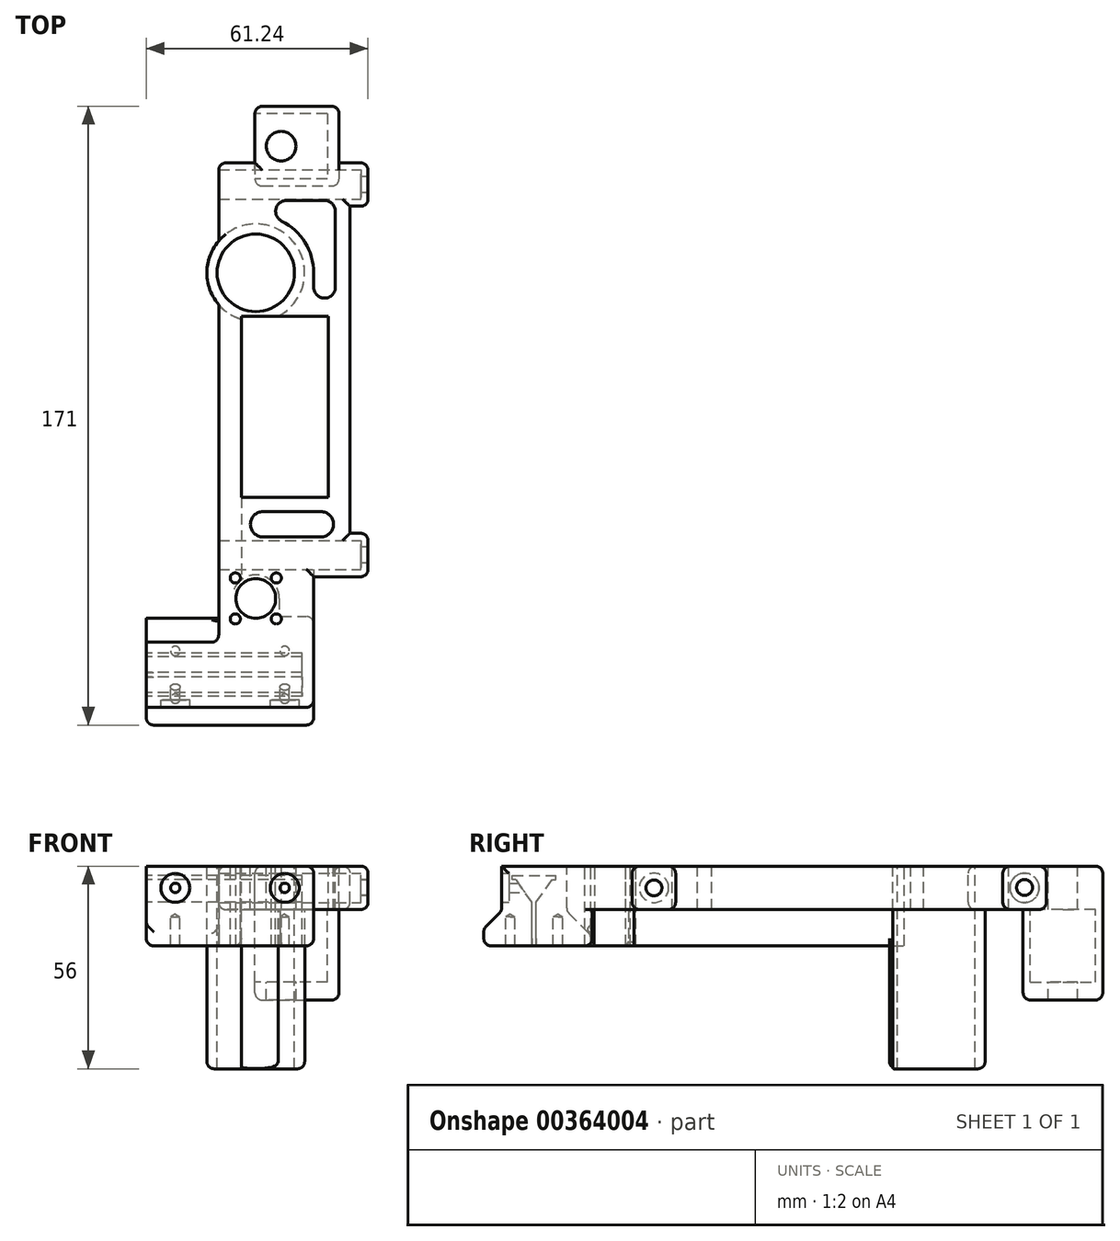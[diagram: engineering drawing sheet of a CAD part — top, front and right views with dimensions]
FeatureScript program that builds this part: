
annotation { "Feature Type Name" : "Feature", "Feature Type Description" : "" }
export const myFeature = defineFeature(function(context is Context, id is Id, definition is map)
    precondition{}
    {
        {
            var Q0;
            Q0=qCreatedBy(makeId("Top.planeOp"),FACE);
            var sketch = newSketch(context, id + "F0", { "sketchPlane" : qUnion([Q0])});
            skLineSegment(sketch, "E0", {"start": v(0, 0) * mm, "end": v(0, -35) * mm});
            skLineSegment(sketch, "E1.bottom", {"start": v(-30, 25) * mm, "end": v(-6, 25) * mm});
            skLineSegment(sketch, "E1.top", {"start": v(-30, -25) * mm, "end": v(-6, -25) * mm});
            skLineSegment(sketch, "E1.left", {"start": v(-30, 25) * mm, "end": v(-30, -25) * mm});
            skLineSegment(sketch, "E1.right", {"start": v(-6, 25) * mm, "end": v(-6, -25) * mm});
            skCircle(sketch, "E2", {"center": v(-26, 37) * mm, "radius": 10.7 * mm});
            skCircle(sketch, "E3", {"center": v(-26, -53) * mm, "radius": 5.5 * mm});
            skLineSegment(sketch, "E4", {"start": v(-10, -47) * mm, "end": v(-10, -88) * mm});
            skLineSegment(sketch, "E5", {"start": v(0, -35) * mm, "end": v(3, -35) * mm});
            skLineSegment(sketch, "E6", {"start": v(3, -35) * mm, "end": v(3, -47) * mm});
            skLineSegment(sketch, "E7", {"start": v(3, -47) * mm, "end": v(-10, -47) * mm});
            skLineSegment(sketch, "E8", {"start": v(3, 67.4) * mm, "end": v(3, 55.4) * mm});
            skLineSegment(sketch, "E9", {"start": v(3, 55.4) * mm, "end": v(0, 55.4) * mm});
            skLineSegment(sketch, "E10", {"start": v(0, 55.4) * mm, "end": v(0, 0) * mm});
            skLineSegment(sketch, "E11", {"start": v(3, 61.4) * mm, "end": v(-99.75, 61.4) * mm, "construction": true});
            skArc(sketch, "E12", {"start": v(-36.24, 28.2) * mm, "mid": v(-39.5, 37) * mm, "end": v(-36.24, 45.8) * mm});
            skLineSegment(sketch, "E13", {"start": v(-36.24, -53) * mm, "end": v(-36.24, 28.2) * mm});
            skLineSegment(sketch, "E14", {"start": v(-36.24, 45.8) * mm, "end": v(-36.24, 67.4) * mm});
            skLineSegment(sketch, "E15", {"start": v(-26.24, 83) * mm, "end": v(-3, 83) * mm});
            skLineSegment(sketch, "E16", {"start": v(-3, 83) * mm, "end": v(-3, 67.4) * mm});
            skLineSegment(sketch, "E17", {"start": v(-3, 67.4) * mm, "end": v(3, 67.4) * mm});
            skLineSegment(sketch, "E18", {"start": v(-36.24, 67.4) * mm, "end": v(-26.24, 67.4) * mm});
            skLineSegment(sketch, "E19", {"start": v(-26.24, 67.4) * mm, "end": v(-26.24, 83) * mm});
            skLineSegment(sketch, "E20", {"start": v(-10, -88) * mm, "end": v(-56.24, -88) * mm});
            skLineSegment(sketch, "E21", {"start": v(-56.24, -88) * mm, "end": v(-56.24, -53) * mm});
            skLineSegment(sketch, "E22", {"start": v(-56.24, -53) * mm, "end": v(-36.24, -53) * mm});
            skLineSegment(sketch, "E23", {"start": v(3, -41) * mm, "end": v(-100.11, -41) * mm, "construction": true});
            skCircle(sketch, "E24", {"center": v(-20.34, -47.34) * mm, "radius": 1.4 * mm});
            skLineSegment(sketch, "E25", {"start": v(-26, -53) * mm, "end": v(-20.34, -47.34) * mm, "construction": true});
            skCircle(sketch, "E26.1.0", {"center": v(-31.66, -47.34) * mm, "radius": 1.4 * mm});
            skLineSegment(sketch, "E26.1.1", {"start": v(-26, -53) * mm, "end": v(-31.66, -47.34) * mm, "construction": true});
            skCircle(sketch, "E26.2.0", {"center": v(-31.66, -58.66) * mm, "radius": 1.4 * mm});
            skLineSegment(sketch, "E26.2.1", {"start": v(-26, -53) * mm, "end": v(-31.66, -58.66) * mm, "construction": true});
            skCircle(sketch, "E26.3.0", {"center": v(-20.34, -58.66) * mm, "radius": 1.4 * mm});
            skLineSegment(sketch, "E26.3.1", {"start": v(-26, -53) * mm, "end": v(-20.34, -58.66) * mm, "construction": true});
            skLineSegment(sketch, "E27.bottom", {"start": v(-24, -36) * mm, "end": v(-8, -36) * mm});
            skLineSegment(sketch, "E27.top", {"start": v(-24, -29) * mm, "end": v(-8, -29) * mm});
            skArc(sketch, "E28", {"start": v(-24, -36) * mm, "mid": v(-27.5, -32.5) * mm, "end": v(-24, -29) * mm});
            skArc(sketch, "E29", {"start": v(-8, -36) * mm, "mid": v(-4.5, -32.5) * mm, "end": v(-8, -29) * mm});
            skArc(sketch, "E30", {"start": v(-4.04, 33.46) * mm, "mid": v(-6.77, 30) * mm, "end": v(-10, 33) * mm});
            skLineSegment(sketch, "E31", {"start": v(-10, 33) * mm, "end": v(-10, 37) * mm});
            skLineSegment(sketch, "E32", {"start": v(-4.04, 33.46) * mm, "end": v(-4.04, 54) * mm});
            skArc(sketch, "E33", {"start": v(-18.85, 51.32) * mm, "mid": v(-20.43, 54.69) * mm, "end": v(-17.51, 57) * mm});
            skLineSegment(sketch, "E34", {"start": v(-17.51, 57) * mm, "end": v(-7.04, 57) * mm});
            skArc(sketch, "E35", {"start": v(-7.04, 57) * mm, "mid": v(-4.91, 56.12) * mm, "end": v(-4.04, 54) * mm});
            skArc(sketch, "E36", {"start": v(-18.85, 51.32) * mm, "mid": v(-12.4, 45.42) * mm, "end": v(-10, 37) * mm});
            skCircle(sketch, "E37", {"center": v(-19, 72) * mm, "radius": 4.1 * mm});
            skSolve(sketch);
        }
        {
            var Q0;
            Q0=qSketchRegion(id+"F0",true);
            extrude(context, id + "F1", {"entities" : qUnion([Q0]), "oppositeDirection" : true, "depth" : 12 * mm, "offsetDistance" : 25 * mm});
        }
        {
            var Q0;
            Q0=makeQuery(id+"F1.opExtrude","SWEPT_FACE",FACE,{"disambiguationData":[OSD([sQuery(id+"F0.wireOp",EDGE,"E6")])]});
            var sketch = newSketch(context, id + "F2", { "sketchPlane" : qUnion([Q0])});
            skCircle(sketch, "E38", {"center": v(-41, -6) * mm, "radius": 4.05 * mm});
            skPoint(sketch, "E38.centerSnap0", {"position": v(-41, 0) * mm});
            skPoint(sketch, "E38.centerSnap1", {"position": v(-47, -6) * mm});
            skCircle(sketch, "E39", {"center": v(61.4, -6) * mm, "radius": 4.05 * mm});
            skPoint(sketch, "E39.centerSnap0", {"position": v(-35, -6) * mm});
            skSolve(sketch);
        }
        {
            var Q0;
            Q0=qSketchRegion(id+"F2",true);
            extrude(context, id + "F3", {"entities" : qUnion([Q0]), "operationType" : NewBodyOperationType.REMOVE, "endBound" : BoundingType.THROUGH_ALL, "oppositeDirection" : true, "depth" : 25 * mm});
        }
        {
            var Q0;
            Q0=makeQuery(id+"F1.opExtrude","SWEPT_FACE",FACE,{"disambiguationData":[OSD([sQuery(id+"F0.wireOp",EDGE,"E6")])]});
            var sketch = newSketch(context, id + "F4", { "sketchPlane" : qUnion([Q0])});
            skLineSegment(sketch, "E40.bottom", {"start": v(-47, 0) * mm, "end": v(-35, 0) * mm});
            skLineSegment(sketch, "E40.top", {"start": v(-47, -12) * mm, "end": v(-35, -12) * mm});
            skLineSegment(sketch, "E40.left", {"start": v(-47, 0) * mm, "end": v(-47, -12) * mm});
            skLineSegment(sketch, "E40.right", {"start": v(-35, 0) * mm, "end": v(-35, -12) * mm});
            skLineSegment(sketch, "E41.bottom", {"start": v(55.4, -12) * mm, "end": v(67.4, -12) * mm});
            skLineSegment(sketch, "E41.top", {"start": v(55.4, 0) * mm, "end": v(67.4, 0) * mm});
            skLineSegment(sketch, "E41.left", {"start": v(55.4, -12) * mm, "end": v(55.4, 0) * mm});
            skLineSegment(sketch, "E41.right", {"start": v(67.4, -12) * mm, "end": v(67.4, 0) * mm});
            skCircle(sketch, "E42", {"center": v(-41, -6) * mm, "radius": 2.2 * mm});
            skCircle(sketch, "E43", {"center": v(61.4, -5.9) * mm, "radius": 2.2 * mm});
            skSolve(sketch);
        }
        {
            var Q0;
            Q0=qSketchRegion(id+"F4",true);
            extrude(context, id + "F5", {"entities" : qUnion([Q0]), "operationType" : NewBodyOperationType.ADD, "depth" : 2 * mm});
        }
        {
            var Q0;
            Q0=makeQuery(id+"F5.boolean.opBoolean","MERGE",FACE,{"derivedFrom":[makeQuery(id+"F1.opExtrude","CAP_FACE",FACE,{"disambiguationData":[OSD([sQuery(id+"F0.wireOp",EDGE,"E0"),sQuery(id+"F0.wireOp",EDGE,"E1.bottom"),sQuery(id+"F0.wireOp",EDGE,"E1.top"),sQuery(id+"F0.wireOp",EDGE,"E1.left"),sQuery(id+"F0.wireOp",EDGE,"E1.right"),sQuery(id+"F0.wireOp",EDGE,"E2"),sQuery(id+"F0.wireOp",EDGE,"E3"),sQuery(id+"F0.wireOp",EDGE,"XIlzzrbo-8YrF-T5Wf-SoYO-HWZPlr7hWIC8"),sQuery(id+"F0.wireOp",EDGE,"E4"),sQuery(id+"F0.wireOp",EDGE,"E5"),sQuery(id+"F0.wireOp",EDGE,"E6"),sQuery(id+"F0.wireOp",EDGE,"E7"),sQuery(id+"F0.wireOp",EDGE,"2jG298rw-YP8h-8Yay-5vSP-wDqkU1IMKlhE"),sQuery(id+"F0.wireOp",EDGE,"E8"),sQuery(id+"F0.wireOp",EDGE,"E9"),sQuery(id+"F0.wireOp",EDGE,"E10"),sQuery(id+"F0.wireOp",EDGE,"SC18iBPG-TUrN-Iioa-Ju5e-pfgaNuiYKQF4"),sQuery(id+"F0.wireOp",EDGE,"QfddEPE0-9GQP-GPq8-b5eB-5ln1efAZQpw0"),sQuery(id+"F0.wireOp",EDGE,"7sLd4AGe-hb9Z-zQUN-UB1L-9xo2n5h3wb6e")])],"isStart":false}),makeQuery(id+"F5.opExtrude","SWEPT_FACE",FACE,{"disambiguationData":[OSD([sQuery(id+"F4.wireOp",EDGE,"E40.top")])]}),makeQuery(id+"F5.opExtrude","SWEPT_FACE",FACE,{"disambiguationData":[OSD([sQuery(id+"F4.wireOp",EDGE,"E41.bottom")])]})]});
            var sketch = newSketch(context, id + "F6", { "sketchPlane" : qUnion([Q0])});
            skLineSegment(sketch, "E44", {"start": v(-19.82, -25) * mm, "end": v(-30, -25) * mm});
            skCircle(sketch, "E45", {"center": v(-26, -37) * mm, "radius": 10.7 * mm});
            skLineSegment(sketch, "E46", {"start": v(-36.24, -28.2) * mm, "end": v(-36.24, -28.2) * mm});
            skArc(sketch, "E47", {"start": v(-19.82, -25) * mm, "mid": v(-23.42, -50.25) * mm, "end": v(-36.24, -28.2) * mm});
            skLineSegment(sketch, "E48", {"start": v(-36.24, -28.2) * mm, "end": v(-36.24, 53) * mm});
            skLineSegment(sketch, "E49", {"start": v(-36.24, 53) * mm, "end": v(-56.24, 53) * mm});
            skLineSegment(sketch, "E50", {"start": v(-56.24, 53) * mm, "end": v(-56.24, 88) * mm});
            skLineSegment(sketch, "E51", {"start": v(-56.24, 88) * mm, "end": v(-10, 88) * mm});
            skLineSegment(sketch, "E52", {"start": v(-10, 88) * mm, "end": v(-10, 58) * mm});
            skLineSegment(sketch, "E53", {"start": v(-30, 47.88) * mm, "end": v(-30, -25) * mm});
            skCircle(sketch, "E54", {"center": v(-26, 53) * mm, "radius": 5.5 * mm});
            skArc(sketch, "E55", {"start": v(-30, 47.88) * mm, "mid": v(-23.15, 47.16) * mm, "end": v(-19.5, 53) * mm});
            skLineSegment(sketch, "E56", {"start": v(-19.5, 53) * mm, "end": v(-19.5, 57.54) * mm});
            skLineSegment(sketch, "E57", {"start": v(-19.1, 58) * mm, "end": v(-10, 58) * mm});
            skCircle(sketch, "E58", {"center": v(-31.66, 58.66) * mm, "radius": 1.4 * mm});
            skCircle(sketch, "E59", {"center": v(-31.66, 47.34) * mm, "radius": 1.4 * mm});
            skArc(sketch, "E60", {"start": v(-19.5, 57.54) * mm, "mid": v(-21.4, 59.57) * mm, "end": v(-19.1, 58) * mm});
            skSolve(sketch);
        }
        {
            var Q0;
            Q0=qSketchRegion(id+"F6",true);
            extrude(context, id + "F7", {"entities" : qUnion([Q0]), "operationType" : NewBodyOperationType.ADD, "depth" : 10 * mm, "offsetDistance" : 25 * mm});
        }
        {
            var Q0;
            Q0=makeQuery(id+"F7.opExtrude","CAP_FACE",FACE,{"disambiguationData":[OSD([sQuery(id+"F6.wireOp",EDGE,"6GX7EmJv-jwu0-vBWY-FxLW-R2JSKk5cSaNS"),sQuery(id+"F6.wireOp",EDGE,"E44"),sQuery(id+"F6.wireOp",EDGE,"hchj6tDb-mTsj-hI8Y-6XvQ-siWjQFpiHixI"),sQuery(id+"F6.wireOp",EDGE,"jRI5jhwU-Cl4Y-UO73-bT4B-RttWuhhWPOQr"),sQuery(id+"F6.wireOp",EDGE,"E45"),sQuery(id+"F6.wireOp",EDGE,"EboCQFRa-d3EB-sAKS-RsI5-4XPLM2VXSoXr"),sQuery(id+"F6.wireOp",EDGE,"GLrA7Uhn-oGKT-5vrt-4Lsz-RlGKhm1cIkbv"),sQuery(id+"F6.wireOp",EDGE,"iAbHuVxw-Mz87-is6H-xszH-xwFxznPorsnN"),sQuery(id+"F6.wireOp",EDGE,"boATnbXS-9fhP-6PQb-uzRW-Yihyjwh3bqXk"),sQuery(id+"F6.wireOp",EDGE,"SkgAi7Z9-kDo3-rvMO-CMYk-elsrKzZPDKzr"),sQuery(id+"F6.wireOp",EDGE,"9utY1JgT-HuLY-Yqt8-Up9m-p6niSZGJffs8"),sQuery(id+"F6.wireOp",EDGE,"Q8Ah0BUv-GUdk-BIgZ-kX4k-YRNa6w1N2wjC"),sQuery(id+"F6.wireOp",EDGE,"4O1aqaJq-Fub8-MtC8-jOK8-P5grKxW9meOc"),sQuery(id+"F6.wireOp",EDGE,"lIdf07tD-03wC-Cnkd-RmJ2-D04lD4p26Tqx"),sQuery(id+"F6.wireOp",EDGE,"E46")])],"isStart":false});
            var sketch = newSketch(context, id + "F8", { "sketchPlane" : qUnion([Q0])});
            skLineSegment(sketch, "E61", {"start": v(-30, -24.1) * mm, "end": v(-30, -25) * mm});
            skLineSegment(sketch, "E62", {"start": v(-30, -25) * mm, "end": v(-19.82, -25) * mm});
            skCircle(sketch, "E63", {"center": v(-26, -37) * mm, "radius": 10.7 * mm});
            skArc(sketch, "E64", {"start": v(-19.82, -25) * mm, "mid": v(-27.18, -50.45) * mm, "end": v(-30, -24.1) * mm});
            skSolve(sketch);
        }
        {
            var Q0;
            Q0=qSketchRegion(id+"F8",true);
            extrude(context, id + "F9", {"entities" : qUnion([Q0]), "operationType" : NewBodyOperationType.ADD, "depth" : 34 * mm, "offsetDistance" : 25 * mm});
        }
        {
            var Q0;
            Q0=makeQuery(id+"F7.boolean.opBoolean","MERGE",FACE,{"derivedFrom":[makeQuery(id+"F1.opExtrude","SWEPT_FACE",FACE,{"disambiguationData":[OSD([sQuery(id+"F0.wireOp",EDGE,"E21")])]}),makeQuery(id+"F7.opExtrude","SWEPT_FACE",FACE,{"disambiguationData":[OSD([sQuery(id+"F6.wireOp",EDGE,"E50")])]})]});
            var sketch = newSketch(context, id + "F10", { "sketchPlane" : qUnion([Q0])});
            skLineSegment(sketch, "E65", {"start": v(74.1, -22) * mm, "end": v(74.1, 0) * mm, "construction": true});
            skLineSegment(sketch, "E66", {"start": v(73.5, -22) * mm, "end": v(73.5, -10) * mm});
            skLineSegment(sketch, "E67", {"start": v(73.5, -10) * mm, "end": v(69.1, -3.7) * mm});
            skLineSegment(sketch, "E68", {"start": v(69.1, -3.7) * mm, "end": v(68.1, -3.7) * mm});
            skLineSegment(sketch, "E69", {"start": v(68.1, -3.7) * mm, "end": v(68.1, -2.6) * mm});
            skLineSegment(sketch, "E70", {"start": v(68.1, -2.6) * mm, "end": v(74.1, -2.6) * mm});
            skLineSegment(sketch, "E71", {"start": v(73.5, -22) * mm, "end": v(74.1, -22) * mm});
            skLineSegment(sketch, "E72.MirrorCS", {"start": v(74.7, -22) * mm, "end": v(74.1, -22) * mm});
            skLineSegment(sketch, "E73.MirrorCS", {"start": v(74.7, -22) * mm, "end": v(74.7, -10) * mm});
            skLineSegment(sketch, "E74.MirrorCS", {"start": v(74.7, -10) * mm, "end": v(79.1, -3.7) * mm});
            skLineSegment(sketch, "E75.MirrorCS", {"start": v(79.1, -3.7) * mm, "end": v(80.1, -3.7) * mm});
            skLineSegment(sketch, "E76.MirrorCS", {"start": v(80.1, -3.7) * mm, "end": v(80.1, -2.6) * mm});
            skLineSegment(sketch, "E77.MirrorCS", {"start": v(80.1, -2.6) * mm, "end": v(74.1, -2.6) * mm});
            skSolve(sketch);
        }
        {
            var Q0;
            Q0=qSketchRegion(id+"F10",true);
            extrude(context, id + "F11", {"entities" : qUnion([Q0]), "operationType" : NewBodyOperationType.REMOVE, "oppositeDirection" : true, "depth" : 43 * mm, "offsetDistance" : 25 * mm});
        }
        {
            var Q0;
            Q0=makeQuery(id+"F7.boolean.opBoolean","MERGE",FACE,{"derivedFrom":[makeQuery(id+"F1.opExtrude","SWEPT_FACE",FACE,{"disambiguationData":[OSD([sQuery(id+"F0.wireOp",EDGE,"E21")])]}),makeQuery(id+"F7.opExtrude","SWEPT_FACE",FACE,{"disambiguationData":[OSD([sQuery(id+"F6.wireOp",EDGE,"E50")])]})]});
            var sketch = newSketch(context, id + "F12", { "sketchPlane" : qUnion([Q0])});
            skLineSegment(sketch, "E78", {"start": v(65.1, -12.4) * mm, "end": v(65.1, 0) * mm});
            skLineSegment(sketch, "E79", {"start": v(65.1, 0) * mm, "end": v(53, 0) * mm});
            skLineSegment(sketch, "E80", {"start": v(53, 0) * mm, "end": v(53, -22) * mm});
            skLineSegment(sketch, "E81", {"start": v(65.1, -12.4) * mm, "end": v(58.5, -19) * mm});
            skLineSegment(sketch, "E82", {"start": v(58.5, -19) * mm, "end": v(58.5, -22) * mm});
            skLineSegment(sketch, "E83", {"start": v(58.5, -22) * mm, "end": v(53, -22) * mm});
            skSolve(sketch);
        }
        {
            var Q0;
            Q0=qSketchRegion(id+"F12",true);
            extrude(context, id + "F13", {"entities" : qUnion([Q0]), "operationType" : NewBodyOperationType.REMOVE, "oppositeDirection" : true, "depth" : 20 * mm, "offsetDistance" : 25 * mm});
        }
        {
            var Q0;
            Q0=makeQuery(id+"F7.boolean.opBoolean","MERGE",FACE,{"derivedFrom":[makeQuery(id+"F1.opExtrude","SWEPT_FACE",FACE,{"disambiguationData":[OSD([sQuery(id+"F0.wireOp",EDGE,"E21")])]}),makeQuery(id+"F7.opExtrude","SWEPT_FACE",FACE,{"disambiguationData":[OSD([sQuery(id+"F6.wireOp",EDGE,"E50")])]})]});
            var sketch = newSketch(context, id + "F14", { "sketchPlane" : qUnion([Q0])});
            skLineSegment(sketch, "E84", {"start": v(88, 0) * mm, "end": v(83.1, 0) * mm});
            skLineSegment(sketch, "E85", {"start": v(83.1, 0) * mm, "end": v(83.1, -12.4) * mm});
            skLineSegment(sketch, "E86", {"start": v(83.1, -12.4) * mm, "end": v(88, -17.3) * mm});
            skLineSegment(sketch, "E87", {"start": v(88, -17.3) * mm, "end": v(88, 0) * mm});
            skSolve(sketch);
        }
        {
            var Q0;
            Q0=qSketchRegion(id+"F14",true);
            extrude(context, id + "F15", {"entities" : qUnion([Q0]), "operationType" : NewBodyOperationType.REMOVE, "endBound" : BoundingType.THROUGH_ALL, "oppositeDirection" : true, "depth" : 25 * mm, "offsetDistance" : 25 * mm});
        }
        {
            var Q0;
            Q0=makeQuery(id+"F5.boolean.opBoolean","MERGE",FACE,{"derivedFrom":[makeQuery(id+"F1.opExtrude","CAP_FACE",FACE,{"disambiguationData":[OSD([sQuery(id+"F0.wireOp",EDGE,"E0"),sQuery(id+"F0.wireOp",EDGE,"E1.bottom"),sQuery(id+"F0.wireOp",EDGE,"E1.top"),sQuery(id+"F0.wireOp",EDGE,"E1.left"),sQuery(id+"F0.wireOp",EDGE,"E1.right"),sQuery(id+"F0.wireOp",EDGE,"E2"),sQuery(id+"F0.wireOp",EDGE,"E3"),sQuery(id+"F0.wireOp",EDGE,"E4"),sQuery(id+"F0.wireOp",EDGE,"E5"),sQuery(id+"F0.wireOp",EDGE,"E6"),sQuery(id+"F0.wireOp",EDGE,"E7"),sQuery(id+"F0.wireOp",EDGE,"E8"),sQuery(id+"F0.wireOp",EDGE,"E9"),sQuery(id+"F0.wireOp",EDGE,"E10"),sQuery(id+"F0.wireOp",EDGE,"E12"),sQuery(id+"F0.wireOp",EDGE,"E13"),sQuery(id+"F0.wireOp",EDGE,"E14"),sQuery(id+"F0.wireOp",EDGE,"E15"),sQuery(id+"F0.wireOp",EDGE,"E16"),sQuery(id+"F0.wireOp",EDGE,"E17"),sQuery(id+"F0.wireOp",EDGE,"E18"),sQuery(id+"F0.wireOp",EDGE,"E19"),sQuery(id+"F0.wireOp",EDGE,"E20"),sQuery(id+"F0.wireOp",EDGE,"E21"),sQuery(id+"F0.wireOp",EDGE,"E22"),sQuery(id+"F0.wireOp",EDGE,"LONgWOeV-YsRU-4v6y-UoGe-SQiEhTrVwKo3"),sQuery(id+"F0.wireOp",EDGE,"E24"),sQuery(id+"F0.wireOp",EDGE,"E26.1.0"),sQuery(id+"F0.wireOp",EDGE,"E26.2.0"),sQuery(id+"F0.wireOp",EDGE,"E26.3.0"),sQuery(id+"F0.wireOp",EDGE,"E27.bottom"),sQuery(id+"F0.wireOp",EDGE,"E27.top"),sQuery(id+"F0.wireOp",EDGE,"E28"),sQuery(id+"F0.wireOp",EDGE,"E29"),sQuery(id+"F0.wireOp",EDGE,"E30"),sQuery(id+"F0.wireOp",EDGE,"E31"),sQuery(id+"F0.wireOp",EDGE,"E32"),sQuery(id+"F0.wireOp",EDGE,"E33"),sQuery(id+"F0.wireOp",EDGE,"E34"),sQuery(id+"F0.wireOp",EDGE,"E35"),sQuery(id+"F0.wireOp",EDGE,"E36")])],"isStart":false}),makeQuery(id+"F5.opExtrude","SWEPT_FACE",FACE,{"disambiguationData":[OSD([sQuery(id+"F4.wireOp",EDGE,"E40.top")])]}),makeQuery(id+"F5.opExtrude","SWEPT_FACE",FACE,{"disambiguationData":[OSD([sQuery(id+"F4.wireOp",EDGE,"E41.bottom")])]})]});
            var sketch = newSketch(context, id + "F16", { "sketchPlane" : qUnion([Q0])});
            skLineSegment(sketch, "E88.bottom", {"start": v(-26.24, -83) * mm, "end": v(-3, -83) * mm});
            skLineSegment(sketch, "E88.top", {"start": v(-26.24, -61) * mm, "end": v(-3, -61) * mm});
            skLineSegment(sketch, "E88.left", {"start": v(-26.24, -83) * mm, "end": v(-26.24, -61) * mm});
            skLineSegment(sketch, "E88.right", {"start": v(-3, -83) * mm, "end": v(-3, -61) * mm});
            skCircle(sketch, "E89", {"center": v(-19, -72) * mm, "radius": 4.1 * mm});
            skSolve(sketch);
        }
        {
            var Q0;
            Q0=qSketchRegion(id+"F16",true);
            extrude(context, id + "F17", {"entities" : qUnion([Q0]), "operationType" : NewBodyOperationType.ADD, "depth" : 25 * mm, "offsetDistance" : 25 * mm});
        }
        {
            var Q0;
            Q0=makeQuery(id+"F17.boolean.opBoolean","MERGE",FACE,{"derivedFrom":[makeQuery(id+"F1.opExtrude","SWEPT_FACE",FACE,{"disambiguationData":[OSD([sQuery(id+"F0.wireOp",EDGE,"E19")])]}),makeQuery(id+"F17.opExtrude","SWEPT_FACE",FACE,{"disambiguationData":[OSD([sQuery(id+"F16.wireOp",EDGE,"E88.left")])]})]});
            var sketch = newSketch(context, id + "F18", { "sketchPlane" : qUnion([Q0])});
            skLineSegment(sketch, "E90.bottom", {"start": v(-63, -32) * mm, "end": v(-81, -32) * mm});
            skLineSegment(sketch, "E90.top", {"start": v(-63, -12) * mm, "end": v(-81, -12) * mm});
            skLineSegment(sketch, "E90.left", {"start": v(-63, -32) * mm, "end": v(-63, -12) * mm});
            skLineSegment(sketch, "E90.right", {"start": v(-81, -32) * mm, "end": v(-81, -12) * mm});
            skPoint(sketch, "E90.middle", {"position": v(-72, -22) * mm});
            skPoint(sketch, "E90.middle.positionSnap0", {"position": v(-72, -37) * mm});
            skPoint(sketch, "E90.centerSnap0", {"position": v(-72, -37) * mm});
            skSolve(sketch);
        }
        {
            var Q0;
            Q0=qSketchRegion(id+"F18",true);
            extrude(context, id + "F19", {"entities" : qUnion([Q0]), "operationType" : NewBodyOperationType.REMOVE, "oppositeDirection" : true, "depth" : 20 * mm, "offsetDistance" : 25 * mm});
        }
        {
            var Q0;
            Q0=makeQuery(id+"F5.opExtrude","CAP_EDGE",EDGE,{"disambiguationData":[OSD([sQuery(id+"F4.wireOp",EDGE,"E40.left")])],"isStart":false});
            var Q1;
            Q1=makeQuery(id+"F5.opExtrude","CAP_EDGE",EDGE,{"disambiguationData":[OSD([sQuery(id+"F4.wireOp",EDGE,"E40.right")])],"isStart":false});
            var Q2;
            Q2=makeQuery(id+"F5.opExtrude","CAP_EDGE",EDGE,{"disambiguationData":[OSD([sQuery(id+"F4.wireOp",EDGE,"E41.left")])],"isStart":false});
            var Q3;
            Q3=makeQuery(id+"F5.opExtrude","CAP_EDGE",EDGE,{"disambiguationData":[OSD([sQuery(id+"F4.wireOp",EDGE,"E41.right")])],"isStart":false});
            var Q4;
            Q4=makeQuery(id+"F1.opExtrude","SWEPT_EDGE",EDGE,{"disambiguationData":[OSD([sQuery(id+"F0.wireOp",EDGE,"E15"),sQuery(id+"F0.wireOp",EDGE,"E19")])]});
            var Q5;
            Q5=makeQuery(id+"F5.boolean.opBoolean","MERGE",EDGE,{"derivedFrom":[makeQuery(id+"F1.opExtrude","CAP_EDGE",EDGE,{"disambiguationData":[OSD([sQuery(id+"F0.wireOp",EDGE,"E17")])],"isStart":true}),makeQuery(id+"F5.opExtrude","SWEPT_EDGE",EDGE,{"disambiguationData":[OSD([sQuery(id+"F4.wireOp",EDGE,"E41.top"),sQuery(id+"F4.wireOp",EDGE,"E41.right")])]})]});
            var Q6;
            Q6=makeQuery(id+"F5.opExtrude","CAP_EDGE",EDGE,{"disambiguationData":[OSD([sQuery(id+"F4.wireOp",EDGE,"E41.top")])],"isStart":false});
            var Q7;
            Q7=makeQuery(id+"F5.boolean.opBoolean","MERGE",EDGE,{"derivedFrom":[makeQuery(id+"F1.opExtrude","CAP_EDGE",EDGE,{"disambiguationData":[OSD([sQuery(id+"F0.wireOp",EDGE,"E9")])],"isStart":true}),makeQuery(id+"F5.opExtrude","SWEPT_EDGE",EDGE,{"disambiguationData":[OSD([sQuery(id+"F4.wireOp",EDGE,"E41.top"),sQuery(id+"F4.wireOp",EDGE,"E41.left")])]})]});
            var Q8;
            Q8=makeQuery(id+"F5.boolean.opBoolean","MERGE",EDGE,{"derivedFrom":[makeQuery(id+"F1.opExtrude","CAP_EDGE",EDGE,{"disambiguationData":[OSD([sQuery(id+"F0.wireOp",EDGE,"E5")])],"isStart":true}),makeQuery(id+"F5.opExtrude","SWEPT_EDGE",EDGE,{"disambiguationData":[OSD([sQuery(id+"F4.wireOp",EDGE,"E40.bottom"),sQuery(id+"F4.wireOp",EDGE,"E40.right")])]})]});
            var Q9;
            Q9=makeQuery(id+"F5.opExtrude","CAP_EDGE",EDGE,{"disambiguationData":[OSD([sQuery(id+"F4.wireOp",EDGE,"E40.bottom")])],"isStart":false});
            var Q10;
            Q10=makeQuery(id+"F5.boolean.opBoolean","MERGE",EDGE,{"derivedFrom":[makeQuery(id+"F1.opExtrude","CAP_EDGE",EDGE,{"disambiguationData":[OSD([sQuery(id+"F0.wireOp",EDGE,"E7")])],"isStart":true}),makeQuery(id+"F5.opExtrude","SWEPT_EDGE",EDGE,{"disambiguationData":[OSD([sQuery(id+"F4.wireOp",EDGE,"E40.bottom"),sQuery(id+"F4.wireOp",EDGE,"E40.left")])]})]});
            var Q11;
            Q11=makeQuery(id+"F13.boolean.opBoolean","MERGE",EDGE,{"derivedFrom":[makeQuery(id+"F1.opExtrude","CAP_EDGE",EDGE,{"disambiguationData":[OSD([sQuery(id+"F0.wireOp",EDGE,"E13")])],"isStart":true}),makeQuery(id+"F13.opExtrude","CAP_EDGE",EDGE,{"disambiguationData":[OSD([sQuery(id+"F12.wireOp",EDGE,"E79")])],"isStart":false})]});
            var Q12;
            Q12=makeQuery(id+"F13.boolean.opBoolean","COPY",EDGE,{"derivedFrom":makeQuery(id+"F13.opExtrude","SWEPT_EDGE",EDGE,{"disambiguationData":[OSD([sQuery(id+"F0.wireOp",EDGE,"E21"),sQuery(id+"F12.wireOp",EDGE,"E78"),sQuery(id+"F12.wireOp",EDGE,"E79")])]})});
            var Q13;
            Q13=makeQuery(id+"F15.boolean.opBoolean","COPY",EDGE,{"derivedFrom":makeQuery(id+"F15.opExtrude","SWEPT_EDGE",EDGE,{"disambiguationData":[OSD([sQuery(id+"F0.wireOp",EDGE,"E21"),sQuery(id+"F14.wireOp",EDGE,"E84"),sQuery(id+"F14.wireOp",EDGE,"E85")])]})});
            var Q14;
            Q14=makeQuery(id+"F13.boolean.opBoolean","MERGE",EDGE,{"derivedFrom":[makeQuery(id+"F7.opExtrude","CAP_EDGE",EDGE,{"disambiguationData":[OSD([sQuery(id+"F6.wireOp",EDGE,"E48")])],"isStart":false}),makeQuery(id+"F13.opExtrude","CAP_EDGE",EDGE,{"disambiguationData":[OSD([sQuery(id+"F12.wireOp",EDGE,"E83")])],"isStart":false})]});
            var Q15;
            Q15=makeQuery(id+"F7.opExtrude","CAP_EDGE",EDGE,{"disambiguationData":[OSD([sQuery(id+"F6.wireOp",EDGE,"E53")])],"isStart":false});
            var Q16;
            Q16=makeQuery(id+"F7.opExtrude","CAP_EDGE",EDGE,{"disambiguationData":[OSD([sQuery(id+"F6.wireOp",EDGE,"E52")])],"isStart":false});
            var Q17;
            Q17=makeQuery(id+"F7.opExtrude","CAP_EDGE",EDGE,{"disambiguationData":[OSD([sQuery(id+"F6.wireOp",EDGE,"E51")])],"isStart":false});
            var Q18;
            {var subQ0=sQuery(id+"F6.wireOp",EDGE,"E50");Q18=makeQuery(id+"F11.boolean.opBoolean","SPLIT",EDGE,{"disambiguationData":[TD([makeQuery(id+"F1.opExtrude","SWEPT_FACE",FACE,{"disambiguationData":[OSD([sQuery(id+"F0.wireOp",EDGE,"E20")])]})])],"derivedFrom":makeQuery(id+"F7.opExtrude","CAP_EDGE",EDGE,{"disambiguationData":[OSD([subQ0])],"isStart":false})});}
            var Q19;
            {var subQ1=sQuery(id+"F6.wireOp",EDGE,"E50");Q19=makeQuery(id+"F11.boolean.opBoolean","SPLIT",EDGE,{"disambiguationData":[TD([makeQuery(id+"F1.opExtrude","SWEPT_FACE",FACE,{"disambiguationData":[OSD([sQuery(id+"F0.wireOp",EDGE,"E22")])]})])],"derivedFrom":makeQuery(id+"F7.opExtrude","CAP_EDGE",EDGE,{"disambiguationData":[OSD([subQ1])],"isStart":false})});}
            var Q20;
            Q20=makeQuery(id+"F7.boolean.opBoolean","MERGE",EDGE,{"derivedFrom":[makeQuery(id+"F1.opExtrude","SWEPT_EDGE",EDGE,{"disambiguationData":[OSD([sQuery(id+"F0.wireOp",EDGE,"E20"),sQuery(id+"F0.wireOp",EDGE,"E21")])]}),makeQuery(id+"F7.opExtrude","SWEPT_EDGE",EDGE,{"disambiguationData":[OSD([sQuery(id+"F6.wireOp",EDGE,"E50"),sQuery(id+"F6.wireOp",EDGE,"E51")])]})]});
            var Q21;
            Q21=makeQuery(id+"F15.boolean.opBoolean","COPY",EDGE,{"derivedFrom":makeQuery(id+"F15.opExtrude","CAP_EDGE",EDGE,{"disambiguationData":[OSD([sQuery(id+"F14.wireOp",EDGE,"E86")])],"isStart":true})});
            var Q22;
            Q22=makeQuery(id+"F15.boolean.opBoolean","COPY",EDGE,{"derivedFrom":makeQuery(id+"F15.opExtrude","SWEPT_EDGE",EDGE,{"disambiguationData":[OSD([sQuery(id+"F14.wireOp",EDGE,"E85"),sQuery(id+"F14.wireOp",EDGE,"E86")])]})});
            var Q23;
            Q23=makeQuery(id+"F7.boolean.opBoolean","MERGE",FACE,{"derivedFrom":[makeQuery(id+"F1.opExtrude","SWEPT_FACE",FACE,{"disambiguationData":[OSD([sQuery(id+"F0.wireOp",EDGE,"E20")])]}),makeQuery(id+"F7.opExtrude","SWEPT_FACE",FACE,{"disambiguationData":[OSD([sQuery(id+"F6.wireOp",EDGE,"E51")])]})]});
            var Q24;
            Q24=makeQuery(id+"F13.boolean.opBoolean","COPY",EDGE,{"derivedFrom":makeQuery(id+"F13.opExtrude","CAP_EDGE",EDGE,{"disambiguationData":[OSD([sQuery(id+"F12.wireOp",EDGE,"E81")])],"isStart":true})});
            var Q25;
            Q25=makeQuery(id+"F13.boolean.opBoolean","COPY",EDGE,{"derivedFrom":makeQuery(id+"F13.opExtrude","CAP_EDGE",EDGE,{"disambiguationData":[OSD([sQuery(id+"F12.wireOp",EDGE,"E78")])],"isStart":true})});
            var Q26;
            Q26=makeQuery(id+"F7.opExtrude","CAP_EDGE",EDGE,{"disambiguationData":[OSD([sQuery(id+"F6.wireOp",EDGE,"E57")])],"isStart":false});
            var Q27;
            Q27=makeQuery(id+"F15.boolean.opBoolean","INTERSECT",EDGE,{"derivedFrom":[makeQuery(id+"F7.boolean.opBoolean","MERGE",FACE,{"derivedFrom":[makeQuery(id+"F1.opExtrude","SWEPT_FACE",FACE,{"disambiguationData":[OSD([sQuery(id+"F0.wireOp",EDGE,"E4")])]}),makeQuery(id+"F7.opExtrude","SWEPT_FACE",FACE,{"disambiguationData":[OSD([sQuery(id+"F6.wireOp",EDGE,"E52")])]})]}),makeQuery(id+"F15.opExtrude","SWEPT_FACE",FACE,{"disambiguationData":[OSD([sQuery(id+"F14.wireOp",EDGE,"E86")])]})]});
            var Q28;
            Q28=makeQuery(id+"F15.boolean.opBoolean","INTERSECT",EDGE,{"derivedFrom":[makeQuery(id+"F7.boolean.opBoolean","MERGE",FACE,{"derivedFrom":[makeQuery(id+"F1.opExtrude","SWEPT_FACE",FACE,{"disambiguationData":[OSD([sQuery(id+"F0.wireOp",EDGE,"E4")])]}),makeQuery(id+"F7.opExtrude","SWEPT_FACE",FACE,{"disambiguationData":[OSD([sQuery(id+"F6.wireOp",EDGE,"E52")])]})]}),makeQuery(id+"F15.opExtrude","SWEPT_FACE",FACE,{"disambiguationData":[OSD([sQuery(id+"F14.wireOp",EDGE,"E85")])]})]});
            var Q29;
            Q29=makeQuery(id+"F13.boolean.opBoolean","COPY",EDGE,{"derivedFrom":makeQuery(id+"F13.opExtrude","SWEPT_EDGE",EDGE,{"disambiguationData":[OSD([sQuery(id+"F12.wireOp",EDGE,"E78"),sQuery(id+"F12.wireOp",EDGE,"E81")])]})});
            var Q30;
            Q30=makeQuery(id+"F13.boolean.opBoolean","COPY",EDGE,{"derivedFrom":makeQuery(id+"F13.opExtrude","CAP_EDGE",EDGE,{"disambiguationData":[OSD([sQuery(id+"F12.wireOp",EDGE,"E81")])],"isStart":false})});
            var Q31;
            Q31=makeQuery(id+"F13.boolean.opBoolean","COPY",EDGE,{"derivedFrom":makeQuery(id+"F13.opExtrude","CAP_EDGE",EDGE,{"disambiguationData":[OSD([sQuery(id+"F12.wireOp",EDGE,"E78")])],"isStart":false})});
            var Q32;
            Q32=makeQuery(id+"F7.opExtrude","CAP_EDGE",EDGE,{"disambiguationData":[OSD([sQuery(id+"F6.wireOp",EDGE,"E47")])],"isStart":true});
            var Q33;
            Q33=makeQuery(id+"F5.boolean.opBoolean","MERGE",EDGE,{"derivedFrom":[makeQuery(id+"F1.opExtrude","CAP_EDGE",EDGE,{"disambiguationData":[OSD([sQuery(id+"F0.wireOp",EDGE,"E9")])],"isStart":false}),makeQuery(id+"F5.opExtrude","SWEPT_EDGE",EDGE,{"disambiguationData":[OSD([sQuery(id+"F4.wireOp",EDGE,"E41.bottom"),sQuery(id+"F4.wireOp",EDGE,"E41.left")])]})]});
            var Q34;
            Q34=makeQuery(id+"F5.opExtrude","CAP_EDGE",EDGE,{"disambiguationData":[OSD([sQuery(id+"F4.wireOp",EDGE,"E41.bottom")])],"isStart":false});
            var Q35;
            Q35=makeQuery(id+"F5.boolean.opBoolean","MERGE",EDGE,{"derivedFrom":[makeQuery(id+"F1.opExtrude","CAP_EDGE",EDGE,{"disambiguationData":[OSD([sQuery(id+"F0.wireOp",EDGE,"E17")])],"isStart":false}),makeQuery(id+"F5.opExtrude","SWEPT_EDGE",EDGE,{"disambiguationData":[OSD([sQuery(id+"F4.wireOp",EDGE,"E41.bottom"),sQuery(id+"F4.wireOp",EDGE,"E41.right")])]})]});
            var Q36;
            Q36=makeQuery(id+"F1.opExtrude","SWEPT_EDGE",EDGE,{"disambiguationData":[OSD([sQuery(id+"F0.wireOp",EDGE,"E15"),sQuery(id+"F0.wireOp",EDGE,"E16")])]});
            var Q37;
            Q37=makeQuery(id+"F5.boolean.opBoolean","MERGE",EDGE,{"derivedFrom":[makeQuery(id+"F1.opExtrude","CAP_EDGE",EDGE,{"disambiguationData":[OSD([sQuery(id+"F0.wireOp",EDGE,"E7")])],"isStart":false}),makeQuery(id+"F5.opExtrude","SWEPT_EDGE",EDGE,{"disambiguationData":[OSD([sQuery(id+"F4.wireOp",EDGE,"E40.top"),sQuery(id+"F4.wireOp",EDGE,"E40.left")])]})]});
            var Q38;
            Q38=makeQuery(id+"F5.opExtrude","CAP_EDGE",EDGE,{"disambiguationData":[OSD([sQuery(id+"F4.wireOp",EDGE,"E40.top")])],"isStart":false});
            var Q39;
            Q39=makeQuery(id+"F5.boolean.opBoolean","MERGE",EDGE,{"derivedFrom":[makeQuery(id+"F1.opExtrude","CAP_EDGE",EDGE,{"disambiguationData":[OSD([sQuery(id+"F0.wireOp",EDGE,"E5")])],"isStart":false}),makeQuery(id+"F5.opExtrude","SWEPT_EDGE",EDGE,{"disambiguationData":[OSD([sQuery(id+"F4.wireOp",EDGE,"E40.top"),sQuery(id+"F4.wireOp",EDGE,"E40.right")])]})]});
            var Q40;
            Q40=makeQuery(id+"F7.opExtrude","CAP_EDGE",EDGE,{"disambiguationData":[OSD([sQuery(id+"F6.wireOp",EDGE,"E53")])],"isStart":true});
            var Q41;
            Q41=makeQuery(id+"F7.opExtrude","CAP_EDGE",EDGE,{"disambiguationData":[OSD([sQuery(id+"F6.wireOp",EDGE,"E55")])],"isStart":true});
            var Q42;
            Q42=makeQuery(id+"F7.opExtrude","CAP_EDGE",EDGE,{"disambiguationData":[OSD([sQuery(id+"F6.wireOp",EDGE,"E57")])],"isStart":true});
            var Q43;
            Q43=makeQuery(id+"F7.opExtrude","SWEPT_EDGE",EDGE,{"disambiguationData":[OSD([sQuery(id+"F0.wireOp",EDGE,"E4"),sQuery(id+"F6.wireOp",EDGE,"E52"),sQuery(id+"F6.wireOp",EDGE,"E57")])]});
            var Q44;
            Q44=makeQuery(id+"F9.opExtrude","CAP_EDGE",EDGE,{"disambiguationData":[OSD([sQuery(id+"F8.wireOp",EDGE,"E64")])],"isStart":false});
            var Q45;
            Q45=makeQuery(id+"F17.opExtrude","CAP_EDGE",EDGE,{"disambiguationData":[OSD([sQuery(id+"F16.wireOp",EDGE,"E88.bottom")])],"isStart":false});
            var Q46;
            Q46=makeQuery(id+"F17.opExtrude","CAP_EDGE",EDGE,{"disambiguationData":[OSD([sQuery(id+"F16.wireOp",EDGE,"E88.right")])],"isStart":false});
            var Q47;
            Q47=makeQuery(id+"F17.opExtrude","CAP_EDGE",EDGE,{"disambiguationData":[OSD([sQuery(id+"F16.wireOp",EDGE,"E88.top")])],"isStart":false});
            var Q48;
            Q48=makeQuery(id+"F17.opExtrude","SWEPT_EDGE",EDGE,{"disambiguationData":[OSD([sQuery(id+"F16.wireOp",EDGE,"E88.top"),sQuery(id+"F16.wireOp",EDGE,"E88.right")])]});
            var Q49;
            Q49=makeQuery(id+"F17.opExtrude","SWEPT_EDGE",EDGE,{"disambiguationData":[OSD([sQuery(id+"F16.wireOp",EDGE,"E88.top"),sQuery(id+"F16.wireOp",EDGE,"E88.left")])]});
            var Q50;
            Q50=makeQuery(id+"F1.opExtrude","CAP_EDGE",EDGE,{"disambiguationData":[OSD([sQuery(id+"F0.wireOp",EDGE,"E14")])],"isStart":false});
            var Q51;
            Q51=makeQuery(id+"F1.opExtrude","CAP_EDGE",EDGE,{"disambiguationData":[OSD([sQuery(id+"F0.wireOp",EDGE,"E18")])],"isStart":false});
            var Q52;
            Q52=makeQuery(id+"F1.opExtrude","SWEPT_EDGE",EDGE,{"disambiguationData":[OSD([sQuery(id+"F0.wireOp",EDGE,"E14"),sQuery(id+"F0.wireOp",EDGE,"E18")])]});
            var Q53;
            Q53=makeQuery(id+"F17.opExtrude","CAP_EDGE",EDGE,{"disambiguationData":[OSD([sQuery(id+"F16.wireOp",EDGE,"E88.top")])],"isStart":true});
            var Q54;
            Q54=makeQuery(id+"F1.opExtrude","CAP_EDGE",EDGE,{"disambiguationData":[OSD([sQuery(id+"F0.wireOp",EDGE,"E0"),sQuery(id+"F0.wireOp",EDGE,"E10")])],"isStart":true});
            var Q55;
            Q55=makeQuery(id+"F1.opExtrude","CAP_EDGE",EDGE,{"disambiguationData":[OSD([sQuery(id+"F0.wireOp",EDGE,"E4")])],"isStart":true});
            var Q56;
            Q56=makeQuery(id+"F1.opExtrude","CAP_EDGE",EDGE,{"disambiguationData":[OSD([sQuery(id+"F0.wireOp",EDGE,"E0"),sQuery(id+"F0.wireOp",EDGE,"E10")])],"isStart":false});
            var Q57;
            Q57=makeQuery(id+"F1.opExtrude","CAP_EDGE",EDGE,{"disambiguationData":[OSD([sQuery(id+"F0.wireOp",EDGE,"E15")])],"isStart":true});
            var Q58;
            Q58=makeQuery(id+"F1.opExtrude","CAP_EDGE",EDGE,{"disambiguationData":[OSD([sQuery(id+"F0.wireOp",EDGE,"E19")])],"isStart":true});
            var Q59;
            Q59=makeQuery(id+"F1.opExtrude","CAP_EDGE",EDGE,{"disambiguationData":[OSD([sQuery(id+"F0.wireOp",EDGE,"E14")])],"isStart":true});
            var Q60;
            Q60=makeQuery(id+"F1.opExtrude","CAP_EDGE",EDGE,{"disambiguationData":[OSD([sQuery(id+"F0.wireOp",EDGE,"E18")])],"isStart":true});
            var Q61;
            Q61=makeQuery(id+"F17.opExtrude","CAP_EDGE",EDGE,{"disambiguationData":[OSD([sQuery(id+"F16.wireOp",EDGE,"E88.left")])],"isStart":false});
            fillet(context, id + "F20", {"entities" : qUnion([Q0, Q1, Q2, Q3, Q4, Q5, Q6, Q7, Q8, Q9, Q10, Q11, Q12, Q13, Q14, Q15, Q16, Q17, Q18, Q19, Q20, Q21, Q22, Q23, Q24, Q25, Q26, Q27, Q28, Q29, Q30, Q31, Q32, Q33, Q34, Q35, Q36, Q37, Q38, Q39, Q40, Q41, Q42, Q43, Q44, Q45, Q46, Q47, Q48, Q49, Q50, Q51, Q52, Q53, Q54, Q55, Q56, Q57, Q58, Q59, Q60, Q61]), "radius" : 2 * mm, "tangentPropagation" : true, "allowEdgeOverflow" : false});
        }
        {
            var Q0;
            Q0=makeQuery(id+"F13.boolean.opBoolean","COPY",EDGE,{"derivedFrom":makeQuery(id+"F13.opExtrude","SWEPT_EDGE",EDGE,{"disambiguationData":[OSD([sQuery(id+"F6.wireOp",EDGE,"E50"),sQuery(id+"F12.wireOp",EDGE,"E82"),sQuery(id+"F12.wireOp",EDGE,"E83")])]})});
            var Q1;
            Q1=makeQuery(id+"F13.boolean.opBoolean","COPY",EDGE,{"derivedFrom":makeQuery(id+"F13.opExtrude","SWEPT_EDGE",EDGE,{"disambiguationData":[OSD([sQuery(id+"F12.wireOp",EDGE,"E81"),sQuery(id+"F12.wireOp",EDGE,"E82")])]})});
            fillet(context, id + "F21", {"entities" : qUnion([Q0, Q1]), "radius" : 1.7 * mm, "tangentPropagation" : true, "allowEdgeOverflow" : false});
        }
        {
            var Q0;
            Q0=makeQuery(id+"F15.boolean.opBoolean","COPY",FACE,{"derivedFrom":makeQuery(id+"F15.opExtrude","SWEPT_FACE",FACE,{"disambiguationData":[OSD([sQuery(id+"F14.wireOp",EDGE,"E85")])]})});
            var sketch = newSketch(context, id + "F22", { "sketchPlane" : qUnion([Q0])});
            skPoint(sketch, "E91", {"position": v(-48.24, -6) * mm});
            skPoint(sketch, "E92", {"position": v(-18, -6) * mm});
            skSolve(sketch);
        }
        {
            var Q0;
            Q0=sQuery(id+"F22.wireOp",VERTEX,"E91");
            var Q1;
            Q1=sQuery(id+"F22.wireOp",VERTEX,"E92");
            var Q2;
            Q2=makeQuery(id+"F1.opExtrude","SWEPT_BODY",BODY,{"disambiguationData":[OSD([sQuery(id+"F0.wireOp",EDGE,"E0"),sQuery(id+"F0.wireOp",EDGE,"E1.bottom"),sQuery(id+"F0.wireOp",EDGE,"E1.top"),sQuery(id+"F0.wireOp",EDGE,"E1.left"),sQuery(id+"F0.wireOp",EDGE,"E1.right"),sQuery(id+"F0.wireOp",EDGE,"E2"),sQuery(id+"F0.wireOp",EDGE,"E3"),sQuery(id+"F0.wireOp",EDGE,"E4"),sQuery(id+"F0.wireOp",EDGE,"E5"),sQuery(id+"F0.wireOp",EDGE,"E6"),sQuery(id+"F0.wireOp",EDGE,"E7"),sQuery(id+"F0.wireOp",EDGE,"E8"),sQuery(id+"F0.wireOp",EDGE,"E9"),sQuery(id+"F0.wireOp",EDGE,"E10"),sQuery(id+"F0.wireOp",EDGE,"E12"),sQuery(id+"F0.wireOp",EDGE,"E13"),sQuery(id+"F0.wireOp",EDGE,"E14"),sQuery(id+"F0.wireOp",EDGE,"E15"),sQuery(id+"F0.wireOp",EDGE,"E16"),sQuery(id+"F0.wireOp",EDGE,"E17"),sQuery(id+"F0.wireOp",EDGE,"E18"),sQuery(id+"F0.wireOp",EDGE,"E19"),sQuery(id+"F0.wireOp",EDGE,"E20"),sQuery(id+"F0.wireOp",EDGE,"E21"),sQuery(id+"F0.wireOp",EDGE,"E22"),sQuery(id+"F0.wireOp",EDGE,"LONgWOeV-YsRU-4v6y-UoGe-SQiEhTrVwKo3")])]});
            hole(context, id + "F23", {"style" : HoleStyle.C_BORE, "endStyle" : HoleEndStyle.BLIND, "holeDiameter" : 2.6 * mm, "cBoreDiameter" : 8 * mm, "cBoreDepth" : 2 * mm, "majorDiameter" : 5 * mm, "holeDepth" : 8 * mm, "isTappedThrough" : true, "tappedDepth" : 12 * mm, "tapClearance" : 3, "locations" : qUnion([Q0, Q1]), "scope" : qUnion([Q2]), "startStyle" : HoleStartStyle.PART});
        }
        {
            var Q0;
            Q0=makeQuery(id+"F7.opExtrude","CAP_FACE",FACE,{"disambiguationData":[OSD([sQuery(id+"F6.wireOp",EDGE,"E44"),sQuery(id+"F6.wireOp",EDGE,"E45"),sQuery(id+"F6.wireOp",EDGE,"E47"),sQuery(id+"F6.wireOp",EDGE,"E48"),sQuery(id+"F6.wireOp",EDGE,"E49"),sQuery(id+"F6.wireOp",EDGE,"E50"),sQuery(id+"F6.wireOp",EDGE,"E51"),sQuery(id+"F6.wireOp",EDGE,"E52"),sQuery(id+"F6.wireOp",EDGE,"E53"),sQuery(id+"F6.wireOp",EDGE,"E54"),sQuery(id+"F6.wireOp",EDGE,"E55"),sQuery(id+"F6.wireOp",EDGE,"E56"),sQuery(id+"F6.wireOp",EDGE,"E57")])],"isStart":false});
            var sketch = newSketch(context, id + "F24", { "sketchPlane" : qUnion([Q0])});
            skPoint(sketch, "E93", {"position": v(-48.24, 80.7) * mm});
            skPoint(sketch, "E94", {"position": v(-18, 80.7) * mm});
            skPoint(sketch, "E95", {"position": v(-48.24, 67.5) * mm});
            skPoint(sketch, "E96", {"position": v(-18, 67.5) * mm});
            skSolve(sketch);
        }
        {
            var Q0;
            Q0=sQuery(id+"F24.wireOp",VERTEX,"E94");
            var Q1;
            Q1=sQuery(id+"F24.wireOp",VERTEX,"E96");
            var Q2;
            Q2=sQuery(id+"F24.wireOp",VERTEX,"E95");
            var Q3;
            Q3=sQuery(id+"F24.wireOp",VERTEX,"E93");
            var Q4;
            Q4=makeQuery(id+"F1.opExtrude","SWEPT_BODY",BODY,{"disambiguationData":[OSD([sQuery(id+"F0.wireOp",EDGE,"E0"),sQuery(id+"F0.wireOp",EDGE,"E1.bottom"),sQuery(id+"F0.wireOp",EDGE,"E1.top"),sQuery(id+"F0.wireOp",EDGE,"E1.left"),sQuery(id+"F0.wireOp",EDGE,"E1.right"),sQuery(id+"F0.wireOp",EDGE,"E2"),sQuery(id+"F0.wireOp",EDGE,"E3"),sQuery(id+"F0.wireOp",EDGE,"E4"),sQuery(id+"F0.wireOp",EDGE,"E5"),sQuery(id+"F0.wireOp",EDGE,"E6"),sQuery(id+"F0.wireOp",EDGE,"E7"),sQuery(id+"F0.wireOp",EDGE,"E8"),sQuery(id+"F0.wireOp",EDGE,"E9"),sQuery(id+"F0.wireOp",EDGE,"E10"),sQuery(id+"F0.wireOp",EDGE,"E12"),sQuery(id+"F0.wireOp",EDGE,"E13"),sQuery(id+"F0.wireOp",EDGE,"E14"),sQuery(id+"F0.wireOp",EDGE,"E15"),sQuery(id+"F0.wireOp",EDGE,"E16"),sQuery(id+"F0.wireOp",EDGE,"E17"),sQuery(id+"F0.wireOp",EDGE,"E18"),sQuery(id+"F0.wireOp",EDGE,"E19"),sQuery(id+"F0.wireOp",EDGE,"E20"),sQuery(id+"F0.wireOp",EDGE,"E21"),sQuery(id+"F0.wireOp",EDGE,"E22"),sQuery(id+"F0.wireOp",EDGE,"LONgWOeV-YsRU-4v6y-UoGe-SQiEhTrVwKo3")])]});
            hole(context, id + "F25", {"style" : HoleStyle.SIMPLE, "endStyle" : HoleEndStyle.BLIND, "holeDiameter" : 2.6 * mm, "majorDiameter" : 5 * mm, "holeDepth" : 8 * mm, "isTappedThrough" : true, "tappedDepth" : 12 * mm, "tapClearance" : 3, "locations" : qUnion([Q0, Q1, Q2, Q3]), "scope" : qUnion([Q4]), "startStyle" : HoleStartStyle.PART});
        }
    });
